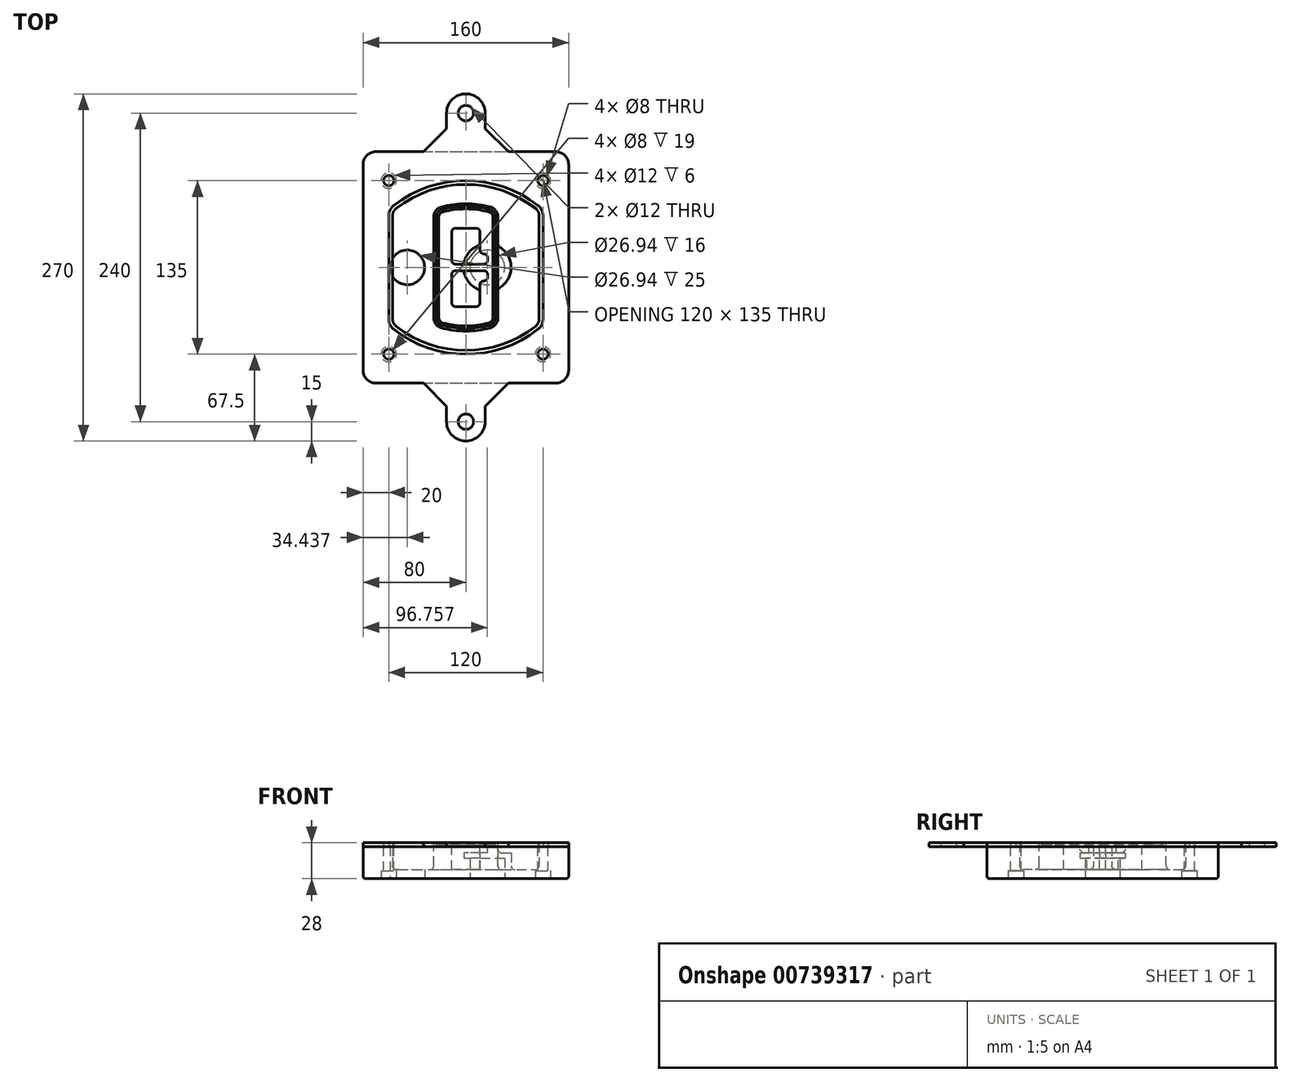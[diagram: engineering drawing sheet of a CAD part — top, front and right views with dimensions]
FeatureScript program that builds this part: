
annotation { "Feature Type Name" : "Feature", "Feature Type Description" : "" }
export const myFeature = defineFeature(function(context is Context, id is Id, definition is map)
    precondition{}
    {
        {
            var Q0;
            Q0=qCreatedBy(makeId("Top.planeOp"),FACE);
            var sketch = newSketch(context, id + "F0", { "sketchPlane" : qUnion([Q0])});
            skPoint(sketch, "E0.rect.middle", {"position": v(0, 0) * mm});
            skLineSegment(sketch, "E1.bottom", {"start": v(-70, -90) * mm, "end": v(70, -90) * mm});
            skLineSegment(sketch, "E1.top", {"start": v(-70, 90) * mm, "end": v(70, 90) * mm});
            skLineSegment(sketch, "E1.left", {"start": v(-80, -80) * mm, "end": v(-80, 80) * mm});
            skLineSegment(sketch, "E1.right", {"start": v(80, -80) * mm, "end": v(80, 80) * mm});
            skLineSegment(sketch, "E2", {"start": v(-80, 90) * mm, "end": v(80, -90) * mm, "construction": true});
            skLineSegment(sketch, "E3", {"start": v(80, 90) * mm, "end": v(-80, -90) * mm, "construction": true});
            skCircle(sketch, "E4", {"center": v(-60, 67.5) * mm, "radius": 4 * mm});
            skCircle(sketch, "E5", {"center": v(60, 67.5) * mm, "radius": 4 * mm});
            skCircle(sketch, "E6", {"center": v(60, -67.5) * mm, "radius": 4 * mm});
            skCircle(sketch, "E7", {"center": v(-60, -67.5) * mm, "radius": 4 * mm});
            skLineSegment(sketch, "E8", {"start": v(-60, 67.5) * mm, "end": v(60, 67.5) * mm, "construction": true});
            skLineSegment(sketch, "E9", {"start": v(60, 67.5) * mm, "end": v(60, -67.5) * mm, "construction": true});
            skLineSegment(sketch, "E10", {"start": v(60, -67.5) * mm, "end": v(-60, -67.5) * mm, "construction": true});
            skLineSegment(sketch, "E11", {"start": v(-60, -67.5) * mm, "end": v(-60, 67.5) * mm, "construction": true});
            skLineSegment(sketch, "E12", {"start": v(-60, 40.3) * mm, "end": v(-60, -40.3) * mm});
            skLineSegment(sketch, "E13", {"start": v(60, 40.3) * mm, "end": v(60, -40.3) * mm});
            skArc(sketch, "E14", {"start": v(56.15, 48.18) * mm, "mid": v(0, 67.5) * mm, "end": v(-56.15, 48.18) * mm});
            skArc(sketch, "E15", {"start": v(-56.15, -48.18) * mm, "mid": v(0, -67.5) * mm, "end": v(56.15, -48.18) * mm});
            skLineSegment(sketch, "E16", {"start": v(-60, 0) * mm, "end": v(60, 0) * mm, "construction": true});
            skPoint(sketch, "E17.visualSharp", {"position": v(-60, -45) * mm});
            skArc(sketch, "E17.filletArc", {"start": v(-60, -40.3) * mm, "mid": v(-58.99, -44.68) * mm, "end": v(-56.15, -48.18) * mm});
            skPoint(sketch, "E18.visualSharp", {"position": v(-60, 45) * mm});
            skArc(sketch, "E18.filletArc", {"start": v(-56.15, 48.18) * mm, "mid": v(-58.99, 44.68) * mm, "end": v(-60, 40.3) * mm});
            skPoint(sketch, "E19.visualSharp", {"position": v(60, 45) * mm});
            skArc(sketch, "E19.filletArc", {"start": v(60, 40.3) * mm, "mid": v(58.99, 44.68) * mm, "end": v(56.15, 48.18) * mm});
            skPoint(sketch, "E20.visualSharp", {"position": v(60, -45) * mm});
            skArc(sketch, "E20.filletArc", {"start": v(56.15, -48.18) * mm, "mid": v(58.99, -44.68) * mm, "end": v(60, -40.3) * mm});
            skPoint(sketch, "E21.visualSharp", {"position": v(-80, 90) * mm});
            skArc(sketch, "E21.filletArc", {"start": v(-70, 90) * mm, "mid": v(-77.07, 87.07) * mm, "end": v(-80, 80) * mm});
            skPoint(sketch, "E22.visualSharp", {"position": v(80, 90) * mm});
            skArc(sketch, "E22.filletArc", {"start": v(80, 80) * mm, "mid": v(77.07, 87.07) * mm, "end": v(70, 90) * mm});
            skPoint(sketch, "E23.visualSharp", {"position": v(80, -90) * mm});
            skArc(sketch, "E23.filletArc", {"start": v(70, -90) * mm, "mid": v(77.07, -87.07) * mm, "end": v(80, -80) * mm});
            skPoint(sketch, "E24.visualSharp", {"position": v(-80, -90) * mm});
            skArc(sketch, "E24.filletArc", {"start": v(-80, -80) * mm, "mid": v(-77.07, -87.07) * mm, "end": v(-70, -90) * mm});
            skArc(sketch, "E25.0", {"start": v(57, 40.3) * mm, "mid": v(56.3, 43.36) * mm, "end": v(54.3, 45.81) * mm});
            skLineSegment(sketch, "E25.1", {"start": v(57, 40.3) * mm, "end": v(57, -40.3) * mm});
            skArc(sketch, "E25.2", {"start": v(54.3, -45.81) * mm, "mid": v(56.3, -43.36) * mm, "end": v(57, -40.3) * mm});
            skArc(sketch, "E25.3", {"start": v(-54.3, -45.81) * mm, "mid": v(0, -64.5) * mm, "end": v(54.3, -45.81) * mm});
            skArc(sketch, "E25.4", {"start": v(-57, -40.3) * mm, "mid": v(-56.3, -43.36) * mm, "end": v(-54.3, -45.81) * mm});
            skArc(sketch, "E25.5", {"start": v(54.3, 45.81) * mm, "mid": v(0, 64.5) * mm, "end": v(-54.3, 45.81) * mm});
            skLineSegment(sketch, "E25.6", {"start": v(-57, 40.3) * mm, "end": v(-57, -40.3) * mm});
            skArc(sketch, "E25.7", {"start": v(-54.3, 45.81) * mm, "mid": v(-56.3, 43.36) * mm, "end": v(-57, 40.3) * mm});
            skArc(sketch, "E26.0", {"start": v(-58.62, 51.33) * mm, "mid": v(-62.58, 46.43) * mm, "end": v(-64, 40.3) * mm});
            skArc(sketch, "E26.1", {"start": v(58.62, 51.33) * mm, "mid": v(0, 71.5) * mm, "end": v(-58.62, 51.33) * mm});
            skArc(sketch, "E26.2", {"start": v(64, 40.3) * mm, "mid": v(62.58, 46.43) * mm, "end": v(58.62, 51.33) * mm});
            skLineSegment(sketch, "E26.3", {"start": v(64, 40.3) * mm, "end": v(64, -40.3) * mm});
            skArc(sketch, "E26.4", {"start": v(58.62, -51.33) * mm, "mid": v(62.58, -46.43) * mm, "end": v(64, -40.3) * mm});
            skLineSegment(sketch, "E26.5", {"start": v(-64, 40.3) * mm, "end": v(-64, -40.3) * mm});
            skArc(sketch, "E26.6", {"start": v(-58.62, -51.33) * mm, "mid": v(0, -71.5) * mm, "end": v(58.62, -51.33) * mm});
            skArc(sketch, "E26.7", {"start": v(-64, -40.3) * mm, "mid": v(-62.58, -46.43) * mm, "end": v(-58.62, -51.33) * mm});
            skSolve(sketch);
        }
        {
            var Q0;
            Q0=makeQuery(id+"F0.imprint","IMPRINT",FACE,{"disambiguationData":[TD([[makeQuery(id+"F0.imprint","IMPRINT",EDGE,{"derivedFrom":sQuery(id+"F0.wireOp",EDGE,"E1.bottom")}),1.0]])]});
            var Q1;
            Q1=makeQuery(id+"F0.imprint","IMPRINT",FACE,{"disambiguationData":[TD([[makeQuery(id+"F0.imprint","IMPRINT",EDGE,{"derivedFrom":sQuery(id+"F0.wireOp",EDGE,"E12")}),1.0]])]});
            var Q2;
            Q2=makeQuery(id+"F0.imprint","IMPRINT",FACE,{"disambiguationData":[TD([[makeQuery(id+"F0.imprint","IMPRINT",EDGE,{"derivedFrom":sQuery(id+"F0.wireOp",EDGE,"E25.0")}),1.0]])]});
            var Q3;
            Q3=makeQuery(id+"F0.imprint","IMPRINT",FACE,{"disambiguationData":[TD([[makeQuery(id+"F0.imprint","IMPRINT",EDGE,{"derivedFrom":sQuery(id+"F0.wireOp",EDGE,"E12")}),-1.0]])]});
            extrude(context, id + "F1", {"entities" : qUnion([Q0, Q1, Q2, Q3]), "oppositeDirection" : true, "depth" : 25 * mm});
        }
        {
            var Q0;
            Q0=makeQuery(id+"F0.imprint","IMPRINT",FACE,{"disambiguationData":[TD([[makeQuery(id+"F0.imprint","IMPRINT",EDGE,{"derivedFrom":sQuery(id+"F0.wireOp",EDGE,"E12")}),1.0]])]});
            extrude(context, id + "F2", {"entities" : qUnion([Q0]), "operationType" : NewBodyOperationType.ADD, "depth" : 3 * mm});
        }
        {
            var Q0;
            Q0=makeQuery(id+"F0.imprint","IMPRINT",FACE,{"disambiguationData":[TD([[makeQuery(id+"F0.imprint","IMPRINT",EDGE,{"derivedFrom":sQuery(id+"F0.wireOp",EDGE,"E25.0")}),1.0]])]});
            extrude(context, id + "F3", {"entities" : qUnion([Q0]), "operationType" : NewBodyOperationType.REMOVE, "oppositeDirection" : true, "depth" : 18 * mm});
        }
        {
            var Q0;
            Q0=makeQuery(id+"F2.opExtrude","CAP_FACE",FACE,{"disambiguationData":[OSD([sQuery(id+"F0.wireOp",EDGE,"E12"),sQuery(id+"F0.wireOp",EDGE,"E13"),sQuery(id+"F0.wireOp",EDGE,"E14"),sQuery(id+"F0.wireOp",EDGE,"E15"),sQuery(id+"F0.wireOp",EDGE,"E17.filletArc"),sQuery(id+"F0.wireOp",EDGE,"E18.filletArc"),sQuery(id+"F0.wireOp",EDGE,"E19.filletArc"),sQuery(id+"F0.wireOp",EDGE,"E20.filletArc"),sQuery(id+"F0.wireOp",EDGE,"E25.0"),sQuery(id+"F0.wireOp",EDGE,"E25.1"),sQuery(id+"F0.wireOp",EDGE,"E25.2"),sQuery(id+"F0.wireOp",EDGE,"E25.3"),sQuery(id+"F0.wireOp",EDGE,"E25.4"),sQuery(id+"F0.wireOp",EDGE,"E25.5"),sQuery(id+"F0.wireOp",EDGE,"E25.6"),sQuery(id+"F0.wireOp",EDGE,"E25.7")])],"isStart":false});
            var sketch = newSketch(context, id + "F4", { "sketchPlane" : qUnion([Q0])});
            skArc(sketch, "E27.0", {"start": v(-19.08, -46.97) * mm, "mid": v(0, -49.5) * mm, "end": v(19.08, -46.97) * mm});
            skArc(sketch, "E28.0", {"start": v(19.08, 46.97) * mm, "mid": v(0, 49.5) * mm, "end": v(-19.08, 46.97) * mm});
            skLineSegment(sketch, "E29", {"start": v(-25, 39.25) * mm, "end": v(-25, -39.25) * mm});
            skLineSegment(sketch, "E30", {"start": v(25, 39.25) * mm, "end": v(25, -39.25) * mm});
            skLineSegment(sketch, "E31", {"start": v(-25, 45.1) * mm, "end": v(25, 45.1) * mm, "construction": true});
            skLineSegment(sketch, "E32", {"start": v(-25, -45.1) * mm, "end": v(25, -45.1) * mm, "construction": true});
            skPoint(sketch, "E33.visualSharp", {"position": v(-25, 45.1) * mm});
            skArc(sketch, "E33.filletArc", {"start": v(-19.08, 46.97) * mm, "mid": v(-23.35, 44.11) * mm, "end": v(-25, 39.25) * mm});
            skPoint(sketch, "E34.visualSharp", {"position": v(25, 45.1) * mm});
            skArc(sketch, "E34.filletArc", {"start": v(25, 39.25) * mm, "mid": v(23.35, 44.11) * mm, "end": v(19.08, 46.97) * mm});
            skPoint(sketch, "E35.visualSharp", {"position": v(25, -45.1) * mm});
            skArc(sketch, "E35.filletArc", {"start": v(19.08, -46.97) * mm, "mid": v(23.35, -44.11) * mm, "end": v(25, -39.25) * mm});
            skPoint(sketch, "E36.visualSharp", {"position": v(-25, -45.1) * mm});
            skArc(sketch, "E36.filletArc", {"start": v(-25, -39.25) * mm, "mid": v(-23.35, -44.11) * mm, "end": v(-19.08, -46.97) * mm});
            skArc(sketch, "E37.0", {"start": v(54.3, 45.81) * mm, "mid": v(0, 64.5) * mm, "end": v(-54.3, 45.81) * mm});
            skArc(sketch, "E37.1", {"start": v(-54.3, 45.81) * mm, "mid": v(-56.3, 43.36) * mm, "end": v(-57, 40.3) * mm});
            skLineSegment(sketch, "E37.2", {"start": v(-57, 40.3) * mm, "end": v(-57, -40.3) * mm});
            skArc(sketch, "E37.3", {"start": v(-57, -40.3) * mm, "mid": v(-56.3, -43.36) * mm, "end": v(-54.3, -45.81) * mm});
            skArc(sketch, "E37.4", {"start": v(-54.3, -45.81) * mm, "mid": v(0, -64.5) * mm, "end": v(54.3, -45.81) * mm});
            skArc(sketch, "E37.5", {"start": v(54.3, -45.81) * mm, "mid": v(56.3, -43.36) * mm, "end": v(57, -40.3) * mm});
            skLineSegment(sketch, "E37.6", {"start": v(57, 40.3) * mm, "end": v(57, -40.3) * mm});
            skArc(sketch, "E37.7", {"start": v(57, 40.3) * mm, "mid": v(56.3, 43.36) * mm, "end": v(54.3, 45.81) * mm});
            skLineSegment(sketch, "E38.0", {"start": v(23, 39.25) * mm, "end": v(23, -39.25) * mm});
            skArc(sketch, "E38.1", {"start": v(18.56, -45.04) * mm, "mid": v(21.76, -42.9) * mm, "end": v(23, -39.25) * mm});
            skArc(sketch, "E38.2", {"start": v(-18.56, -45.04) * mm, "mid": v(0, -47.5) * mm, "end": v(18.56, -45.04) * mm});
            skArc(sketch, "E38.3", {"start": v(-23, -39.25) * mm, "mid": v(-21.76, -42.9) * mm, "end": v(-18.56, -45.04) * mm});
            skLineSegment(sketch, "E38.4", {"start": v(-23, 39.25) * mm, "end": v(-23, -39.25) * mm});
            skArc(sketch, "E38.5", {"start": v(23, 39.25) * mm, "mid": v(21.76, 42.9) * mm, "end": v(18.56, 45.04) * mm});
            skArc(sketch, "E38.6", {"start": v(-18.56, 45.04) * mm, "mid": v(-21.76, 42.9) * mm, "end": v(-23, 39.25) * mm});
            skArc(sketch, "E38.7", {"start": v(18.56, 45.04) * mm, "mid": v(0, 47.5) * mm, "end": v(-18.56, 45.04) * mm});
            skArc(sketch, "E39.0", {"start": v(21, 39.25) * mm, "mid": v(20.18, 41.68) * mm, "end": v(18.04, 43.1) * mm});
            skLineSegment(sketch, "E39.1", {"start": v(21, 39.25) * mm, "end": v(21, -39.25) * mm});
            skArc(sketch, "E39.2", {"start": v(18.04, -43.1) * mm, "mid": v(20.18, -41.68) * mm, "end": v(21, -39.25) * mm});
            skArc(sketch, "E39.3", {"start": v(-18.04, -43.1) * mm, "mid": v(0, -45.5) * mm, "end": v(18.04, -43.1) * mm});
            skArc(sketch, "E39.4", {"start": v(-21, -39.25) * mm, "mid": v(-20.18, -41.68) * mm, "end": v(-18.04, -43.1) * mm});
            skArc(sketch, "E39.5", {"start": v(18.04, 43.1) * mm, "mid": v(0, 45.5) * mm, "end": v(-18.04, 43.1) * mm});
            skLineSegment(sketch, "E39.6", {"start": v(-21, 39.25) * mm, "end": v(-21, -39.25) * mm});
            skArc(sketch, "E39.7", {"start": v(-18.04, 43.1) * mm, "mid": v(-20.18, 41.68) * mm, "end": v(-21, 39.25) * mm});
            skLineSegment(sketch, "E40", {"start": v(-25, 0) * mm, "end": v(25, 0) * mm, "construction": true});
            skLineSegment(sketch, "E41", {"start": v(-11, 5.5) * mm, "end": v(-11, 27.5) * mm});
            skLineSegment(sketch, "E42", {"start": v(-8, 30.5) * mm, "end": v(8, 30.5) * mm});
            skLineSegment(sketch, "E43", {"start": v(11, 27.5) * mm, "end": v(11, 13.5) * mm});
            skLineSegment(sketch, "E44", {"start": v(14, 10.5) * mm, "end": v(14, 10.5) * mm});
            skLineSegment(sketch, "E45", {"start": v(17, 7.5) * mm, "end": v(17, 5.5) * mm});
            skLineSegment(sketch, "E46", {"start": v(14, 2.5) * mm, "end": v(-8, 2.5) * mm});
            skPoint(sketch, "E47.visualSharp", {"position": v(-11, 30.5) * mm});
            skArc(sketch, "E47.filletArc", {"start": v(-8, 30.5) * mm, "mid": v(-10.12, 29.62) * mm, "end": v(-11, 27.5) * mm});
            skPoint(sketch, "E48.visualSharp", {"position": v(11, 30.5) * mm});
            skArc(sketch, "E48.filletArc", {"start": v(11, 27.5) * mm, "mid": v(10.12, 29.62) * mm, "end": v(8, 30.5) * mm});
            skPoint(sketch, "E49.visualSharp", {"position": v(11, 10.5) * mm});
            skArc(sketch, "E49.filletArc", {"start": v(11, 13.5) * mm, "mid": v(11.88, 11.38) * mm, "end": v(14, 10.5) * mm});
            skPoint(sketch, "E50.visualSharp", {"position": v(17, 10.5) * mm});
            skArc(sketch, "E50.filletArc", {"start": v(17, 7.5) * mm, "mid": v(16.12, 9.62) * mm, "end": v(14, 10.5) * mm});
            skPoint(sketch, "E51.visualSharp", {"position": v(17, 2.5) * mm});
            skArc(sketch, "E51.filletArc", {"start": v(14, 2.5) * mm, "mid": v(16.12, 3.38) * mm, "end": v(17, 5.5) * mm});
            skPoint(sketch, "E52.visualSharp", {"position": v(-11, 2.5) * mm});
            skArc(sketch, "E52.filletArc", {"start": v(-11, 5.5) * mm, "mid": v(-10.12, 3.38) * mm, "end": v(-8, 2.5) * mm});
            skLineSegment(sketch, "E53.0.MirrorCS", {"start": v(14, -2.5) * mm, "end": v(-8, -2.5) * mm});
            skArc(sketch, "E54.0.MirrorCS", {"start": v(-11, -5.5) * mm, "mid": v(-10.12, -3.38) * mm, "end": v(-8, -2.5) * mm});
            skLineSegment(sketch, "E55.0.MirrorCS", {"start": v(-11, -5.5) * mm, "end": v(-11, -27.5) * mm});
            skArc(sketch, "E56.0.MirrorCS", {"start": v(-8, -30.5) * mm, "mid": v(-10.12, -29.62) * mm, "end": v(-11, -27.5) * mm});
            skLineSegment(sketch, "E57.0.MirrorCS", {"start": v(-8, -30.5) * mm, "end": v(8, -30.5) * mm});
            skArc(sketch, "E58.0.MirrorCS", {"start": v(11, -27.5) * mm, "mid": v(10.12, -29.62) * mm, "end": v(8, -30.5) * mm});
            skLineSegment(sketch, "E59.0.MirrorCS", {"start": v(11, -27.5) * mm, "end": v(11, -13.5) * mm});
            skArc(sketch, "E60.0.MirrorCS", {"start": v(11, -13.5) * mm, "mid": v(11.88, -11.38) * mm, "end": v(14, -10.5) * mm});
            skArc(sketch, "E61.0.MirrorCS", {"start": v(17, -7.5) * mm, "mid": v(16.12, -9.62) * mm, "end": v(14, -10.5) * mm});
            skLineSegment(sketch, "E62.0.MirrorCS", {"start": v(17, -7.5) * mm, "end": v(17, -5.5) * mm});
            skArc(sketch, "E63.0.MirrorCS", {"start": v(14, -2.5) * mm, "mid": v(16.12, -3.38) * mm, "end": v(17, -5.5) * mm});
            skSolve(sketch);
        }
        {
            var Q0;
            Q0=makeQuery(id+"F4.imprint","IMPRINT",FACE,{"disambiguationData":[TD([[makeQuery(id+"F4.imprint","IMPRINT",EDGE,{"derivedFrom":sQuery(id+"F4.wireOp",EDGE,"E27.0")}),1.0]])]});
            var Q1;
            Q1=makeQuery(id+"F4.imprint","IMPRINT",FACE,{"disambiguationData":[TD([[makeQuery(id+"F4.imprint","IMPRINT",EDGE,{"derivedFrom":sQuery(id+"F4.wireOp",EDGE,"E38.0")}),-1.0]])]});
            var Q2;
            Q2=makeQuery(id+"F4.imprint","IMPRINT",FACE,{"disambiguationData":[TD([[makeQuery(id+"F4.imprint","IMPRINT",EDGE,{"derivedFrom":sQuery(id+"F4.wireOp",EDGE,"E39.0")}),1.0]])]});
            extrude(context, id + "F5", {"entities" : qUnion([Q0, Q1, Q2]), "operationType" : NewBodyOperationType.ADD, "endBound" : BoundingType.UP_TO_NEXT, "oppositeDirection" : true, "depth" : 25 * mm});
        }
        {
            var Q0;
            Q0=makeQuery(id+"F4.imprint","IMPRINT",FACE,{"disambiguationData":[TD([[makeQuery(id+"F4.imprint","IMPRINT",EDGE,{"derivedFrom":sQuery(id+"F4.wireOp",EDGE,"E38.0")}),-1.0]])]});
            extrude(context, id + "F6", {"entities" : qUnion([Q0]), "operationType" : NewBodyOperationType.REMOVE, "oppositeDirection" : true, "depth" : 2 * mm});
        }
        {
            var Q0;
            Q0=makeQuery(id+"F1.opExtrude","CAP_FACE",FACE,{"disambiguationData":[OSD([sQuery(id+"F0.wireOp",EDGE,"E1.bottom"),sQuery(id+"F0.wireOp",EDGE,"E1.top"),sQuery(id+"F0.wireOp",EDGE,"E1.left"),sQuery(id+"F0.wireOp",EDGE,"E1.right"),sQuery(id+"F0.wireOp",EDGE,"E4"),sQuery(id+"F0.wireOp",EDGE,"E5"),sQuery(id+"F0.wireOp",EDGE,"E6"),sQuery(id+"F0.wireOp",EDGE,"E7"),sQuery(id+"F0.wireOp",EDGE,"E21.filletArc"),sQuery(id+"F0.wireOp",EDGE,"E22.filletArc"),sQuery(id+"F0.wireOp",EDGE,"E23.filletArc"),sQuery(id+"F0.wireOp",EDGE,"E24.filletArc")])],"isStart":false});
            var sketch = newSketch(context, id + "F7", { "sketchPlane" : qUnion([Q0])});
            skCircle(sketch, "E64", {"center": v(16.76, 0) * mm, "radius": 13.47 * mm});
            skCircle(sketch, "E65", {"center": v(-45.56, 0) * mm, "radius": 13.47 * mm});
            skLineSegment(sketch, "E66", {"start": v(80, 0) * mm, "end": v(-80, 0) * mm});
            skCircle(sketch, "E67", {"center": v(16.76, 0) * mm, "radius": 18.47 * mm});
            skCircle(sketch, "E68", {"center": v(60, -67.5) * mm, "radius": 6 * mm});
            skCircle(sketch, "E69", {"center": v(-60, -67.5) * mm, "radius": 6 * mm});
            skCircle(sketch, "E70", {"center": v(-60, 67.5) * mm, "radius": 6 * mm});
            skCircle(sketch, "E71", {"center": v(60, 67.5) * mm, "radius": 6 * mm});
            skSolve(sketch);
        }
        {
            var Q0;
            {var subQ1=sQuery(id+"F7.wireOp",EDGE,"E66");var subQ4=sQuery(id+"F7.wireOp",EDGE,"E64");var subQ6=makeQuery(id+"F7.imprint","INTERSECT",VERTEX,{"disambiguationData":[OD(0.0)],"derivedFrom":[subQ4,subQ1]});Q0=makeQuery(id+"F7.imprint","IMPRINT",FACE,{"disambiguationData":[TD([[makeQuery(id+"F7.imprint","IMPRINT",EDGE,{"disambiguationData":[TD([[subQ6,-1.0]])],"derivedFrom":subQ4}),-1.0]])]});}
            var Q1;
            {var subQ0=sQuery(id+"F7.wireOp",EDGE,"E66");var subQ1=sQuery(id+"F7.wireOp",EDGE,"E64");var subQ3=makeQuery(id+"F7.imprint","INTERSECT",VERTEX,{"disambiguationData":[OD(0.0)],"derivedFrom":[subQ1,subQ0]});Q1=makeQuery(id+"F7.imprint","IMPRINT",FACE,{"disambiguationData":[TD([[makeQuery(id+"F7.imprint","IMPRINT",EDGE,{"disambiguationData":[TD([[subQ3,-1.0]])],"derivedFrom":subQ1}),1.0]])]});}
            var Q2;
            {var subQ0=sQuery(id+"F7.wireOp",EDGE,"E66");var subQ1=sQuery(id+"F7.wireOp",EDGE,"E64");var subQ3=makeQuery(id+"F7.imprint","INTERSECT",VERTEX,{"disambiguationData":[OD(0.0)],"derivedFrom":[subQ1,subQ0]});Q2=makeQuery(id+"F7.imprint","IMPRINT",FACE,{"disambiguationData":[TD([[makeQuery(id+"F7.imprint","IMPRINT",EDGE,{"disambiguationData":[TD([[subQ3,1.0]])],"derivedFrom":subQ1}),1.0]])]});}
            var Q3;
            {var subQ1=sQuery(id+"F7.wireOp",EDGE,"E66");var subQ4=sQuery(id+"F7.wireOp",EDGE,"E64");var subQ6=makeQuery(id+"F7.imprint","INTERSECT",VERTEX,{"disambiguationData":[OD(0.0)],"derivedFrom":[subQ4,subQ1]});Q3=makeQuery(id+"F7.imprint","IMPRINT",FACE,{"disambiguationData":[TD([[makeQuery(id+"F7.imprint","IMPRINT",EDGE,{"disambiguationData":[TD([[subQ6,1.0]])],"derivedFrom":subQ4}),-1.0]])]});}
            extrude(context, id + "F8", {"entities" : qUnion([Q0, Q1, Q2, Q3]), "operationType" : NewBodyOperationType.ADD, "oppositeDirection" : true, "depth" : 20 * mm});
        }
        {
            var Q0;
            {var subQ0=sQuery(id+"F7.wireOp",EDGE,"E66");var subQ1=sQuery(id+"F7.wireOp",EDGE,"E64");var subQ3=makeQuery(id+"F7.imprint","INTERSECT",VERTEX,{"disambiguationData":[OD(0.0)],"derivedFrom":[subQ1,subQ0]});Q0=makeQuery(id+"F7.imprint","IMPRINT",FACE,{"disambiguationData":[TD([[makeQuery(id+"F7.imprint","IMPRINT",EDGE,{"disambiguationData":[TD([[subQ3,-1.0]])],"derivedFrom":subQ1}),1.0]])]});}
            var Q1;
            {var subQ0=sQuery(id+"F7.wireOp",EDGE,"E66");var subQ1=sQuery(id+"F7.wireOp",EDGE,"E64");var subQ3=makeQuery(id+"F7.imprint","INTERSECT",VERTEX,{"disambiguationData":[OD(0.0)],"derivedFrom":[subQ1,subQ0]});Q1=makeQuery(id+"F7.imprint","IMPRINT",FACE,{"disambiguationData":[TD([[makeQuery(id+"F7.imprint","IMPRINT",EDGE,{"disambiguationData":[TD([[subQ3,1.0]])],"derivedFrom":subQ1}),1.0]])]});}
            extrude(context, id + "F9", {"entities" : qUnion([Q0, Q1]), "operationType" : NewBodyOperationType.REMOVE, "oppositeDirection" : true, "depth" : 16 * mm});
        }
        {
            var Q0;
            {var subQ0=sQuery(id+"F7.wireOp",EDGE,"E66");var subQ1=sQuery(id+"F7.wireOp",EDGE,"E65");var subQ3=makeQuery(id+"F7.imprint","INTERSECT",VERTEX,{"disambiguationData":[OD(0.0)],"derivedFrom":[subQ1,subQ0]});Q0=makeQuery(id+"F7.imprint","IMPRINT",FACE,{"disambiguationData":[TD([[makeQuery(id+"F7.imprint","IMPRINT",EDGE,{"disambiguationData":[TD([[subQ3,-1.0]])],"derivedFrom":subQ1}),1.0]])]});}
            var Q1;
            {var subQ0=sQuery(id+"F7.wireOp",EDGE,"E66");var subQ1=sQuery(id+"F7.wireOp",EDGE,"E65");var subQ3=makeQuery(id+"F7.imprint","INTERSECT",VERTEX,{"disambiguationData":[OD(0.0)],"derivedFrom":[subQ1,subQ0]});Q1=makeQuery(id+"F7.imprint","IMPRINT",FACE,{"disambiguationData":[TD([[makeQuery(id+"F7.imprint","IMPRINT",EDGE,{"disambiguationData":[TD([[subQ3,1.0]])],"derivedFrom":subQ1}),1.0]])]});}
            extrude(context, id + "F10", {"entities" : qUnion([Q0, Q1]), "operationType" : NewBodyOperationType.REMOVE, "oppositeDirection" : true, "depth" : 25 * mm});
        }
        {
            var Q0;
            Q0=makeQuery(id+"F7.imprint","IMPRINT",FACE,{"disambiguationData":[TD([[makeQuery(id+"F7.imprint","IMPRINT",EDGE,{"derivedFrom":sQuery(id+"F7.wireOp",EDGE,"E68")}),1.0]])]});
            var Q1;
            Q1=makeQuery(id+"F7.imprint","IMPRINT",FACE,{"disambiguationData":[TD([[makeQuery(id+"F7.imprint","IMPRINT",EDGE,{"derivedFrom":makeQuery(id+"F1.opExtrude","CAP_EDGE",EDGE,{"disambiguationData":[OSD([sQuery(id+"F0.wireOp",EDGE,"E5")])],"isStart":false})}),-1.0]])]});
            var Q2;
            Q2=makeQuery(id+"F7.imprint","IMPRINT",FACE,{"disambiguationData":[TD([[makeQuery(id+"F7.imprint","IMPRINT",EDGE,{"derivedFrom":sQuery(id+"F7.wireOp",EDGE,"E69")}),1.0]])]});
            var Q3;
            Q3=makeQuery(id+"F7.imprint","IMPRINT",FACE,{"disambiguationData":[TD([[makeQuery(id+"F7.imprint","IMPRINT",EDGE,{"derivedFrom":makeQuery(id+"F1.opExtrude","CAP_EDGE",EDGE,{"disambiguationData":[OSD([sQuery(id+"F0.wireOp",EDGE,"E4")])],"isStart":false})}),-1.0]])]});
            var Q4;
            Q4=makeQuery(id+"F7.imprint","IMPRINT",FACE,{"disambiguationData":[TD([[makeQuery(id+"F7.imprint","IMPRINT",EDGE,{"derivedFrom":sQuery(id+"F7.wireOp",EDGE,"E70")}),1.0]])]});
            var Q5;
            Q5=makeQuery(id+"F7.imprint","IMPRINT",FACE,{"disambiguationData":[TD([[makeQuery(id+"F7.imprint","IMPRINT",EDGE,{"derivedFrom":makeQuery(id+"F1.opExtrude","CAP_EDGE",EDGE,{"disambiguationData":[OSD([sQuery(id+"F0.wireOp",EDGE,"E7")])],"isStart":false})}),-1.0]])]});
            var Q6;
            Q6=makeQuery(id+"F7.imprint","IMPRINT",FACE,{"disambiguationData":[TD([[makeQuery(id+"F7.imprint","IMPRINT",EDGE,{"derivedFrom":sQuery(id+"F7.wireOp",EDGE,"E71")}),1.0]])]});
            var Q7;
            Q7=makeQuery(id+"F7.imprint","IMPRINT",FACE,{"disambiguationData":[TD([[makeQuery(id+"F7.imprint","IMPRINT",EDGE,{"derivedFrom":makeQuery(id+"F1.opExtrude","CAP_EDGE",EDGE,{"disambiguationData":[OSD([sQuery(id+"F0.wireOp",EDGE,"E6")])],"isStart":false})}),-1.0]])]});
            var Q8;
            Q8 = qSketchRegion(id + "F16", true);
            extrude(context, id + "F11", {"entities" : qUnion([Q0, Q1, Q2, Q3, Q4, Q5, Q6, Q7, Q8]), "operationType" : NewBodyOperationType.REMOVE, "oppositeDirection" : true, "depth" : 6 * mm, "offsetDistance" : 25 * mm});
        }
        {
            var Q0;
            Q0=makeQuery(id+"F9.boolean.opBoolean","COPY",FACE,{"derivedFrom":makeQuery(id+"F9.opExtrude","CAP_FACE",FACE,{"disambiguationData":[OSD([sQuery(id+"F7.wireOp",EDGE,"E64")])],"isStart":false})});
            var sketch = newSketch(context, id + "F12", { "sketchPlane" : qUnion([Q0])});
            skArc(sketch, "E72.0", {"start": v(11, 17.55) * mm, "mid": v(2.57, 11.82) * mm, "end": v(-1.54, 2.5) * mm});
            skArc(sketch, "E72.1", {"start": v(-1.54, -2.5) * mm, "mid": v(2.57, -11.82) * mm, "end": v(11, -17.55) * mm});
            skLineSegment(sketch, "E73", {"start": v(-1.54, -2.5) * mm, "end": v(14, -2.5) * mm});
            skLineSegment(sketch, "E74.0", {"start": v(14, 2.5) * mm, "end": v(-1.54, 2.5) * mm});
            skArc(sketch, "E74.1", {"start": v(14, 2.5) * mm, "mid": v(16.12, 3.38) * mm, "end": v(17, 5.5) * mm});
            skLineSegment(sketch, "E74.2", {"start": v(17, 7.5) * mm, "end": v(17, 5.5) * mm});
            skArc(sketch, "E74.3", {"start": v(17, 7.5) * mm, "mid": v(16.12, 9.62) * mm, "end": v(14, 10.5) * mm});
            skArc(sketch, "E74.4", {"start": v(11, 13.5) * mm, "mid": v(11.88, 11.38) * mm, "end": v(14, 10.5) * mm});
            skLineSegment(sketch, "E74.5", {"start": v(11, 17.55) * mm, "end": v(11, 13.5) * mm});
            skLineSegment(sketch, "E74.7", {"start": v(14, -2.5) * mm, "end": v(-1.54, -2.5) * mm});
            skArc(sketch, "E74.8", {"start": v(14, -2.5) * mm, "mid": v(16.12, -3.38) * mm, "end": v(17, -5.5) * mm});
            skLineSegment(sketch, "E74.9", {"start": v(17, -7.5) * mm, "end": v(17, -5.5) * mm});
            skArc(sketch, "E74.10", {"start": v(17, -7.5) * mm, "mid": v(16.12, -9.62) * mm, "end": v(14, -10.5) * mm});
            skArc(sketch, "E74.11", {"start": v(11, -13.5) * mm, "mid": v(11.88, -11.38) * mm, "end": v(14, -10.5) * mm});
            skLineSegment(sketch, "E74.12", {"start": v(11, -17.55) * mm, "end": v(11, -13.5) * mm});
            skPoint(sketch, "E75.orphan", {"position": v(11, -27.5) * mm});
            skPoint(sketch, "E76.orphan", {"position": v(-8, -2.5) * mm});
            skPoint(sketch, "E77.orphan", {"position": v(-8, 2.5) * mm});
            skPoint(sketch, "E78.orphan", {"position": v(11, 27.5) * mm});
            skSolve(sketch);
        }
        {
            var Q0;
            {var subQ7=sQuery(id+"F12.wireOp",EDGE,"E72.0");var subQ14=sQuery(id+"F12.wireOp",EDGE,"E72.1");var subQ16=sQuery(id+"F12.wireOp",EDGE,"E74.1");var subQ18=sQuery(id+"F12.wireOp",EDGE,"E74.8");Q0=qUnion([makeQuery(id+"F12.imprint","IMPRINT",FACE,{"disambiguationData":[TD([[makeQuery(id+"F12.imprint","IMPRINT",EDGE,{"derivedFrom":subQ7}),1.0]])]}),makeQuery(id+"F12.imprint","IMPRINT",FACE,{"disambiguationData":[TD([[makeQuery(id+"F12.imprint","IMPRINT",EDGE,{"derivedFrom":subQ14}),1.0]])]}),makeQuery(id+"F12.imprint","IMPRINT",FACE,{"disambiguationData":[TD([[makeQuery(id+"F12.imprint","IMPRINT",EDGE,{"derivedFrom":subQ16}),1.0]])]}),makeQuery(id+"F12.imprint","IMPRINT",FACE,{"disambiguationData":[TD([[makeQuery(id+"F12.imprint","IMPRINT",EDGE,{"derivedFrom":subQ18}),-1.0]])]})]);}
            var Q1;
            Q1=makeQuery(id+"F5.boolean.opBoolean","SPLIT",FACE,{"disambiguationData":[TD([makeQuery(id+"F5.opExtrude","SWEPT_FACE",FACE,{"disambiguationData":[OSD([sQuery(id+"F4.wireOp",EDGE,"E41")])]})])],"derivedFrom":makeQuery(id+"F3.boolean.opBoolean","COPY",FACE,{"derivedFrom":makeQuery(id+"F3.opExtrude","CAP_FACE",FACE,{"disambiguationData":[OSD([sQuery(id+"F0.wireOp",EDGE,"E25.0"),sQuery(id+"F0.wireOp",EDGE,"E25.1"),sQuery(id+"F0.wireOp",EDGE,"E25.2"),sQuery(id+"F0.wireOp",EDGE,"E25.3"),sQuery(id+"F0.wireOp",EDGE,"E25.4"),sQuery(id+"F0.wireOp",EDGE,"E25.5"),sQuery(id+"F0.wireOp",EDGE,"E25.6"),sQuery(id+"F0.wireOp",EDGE,"E25.7")])],"isStart":false})})});
            extrude(context, id + "F13", {"entities" : qUnion([Q0]), "operationType" : NewBodyOperationType.REMOVE, "endBound" : BoundingType.UP_TO_SURFACE, "endBoundEntityFace" : qUnion([Q1]), "depth" : 25 * mm});
        }
        {
            var Q0;
            Q0=makeQuery(id+"F3.boolean.opBoolean","COPY",EDGE,{"derivedFrom":makeQuery(id+"F3.opExtrude","CAP_EDGE",EDGE,{"disambiguationData":[OSD([sQuery(id+"F0.wireOp",EDGE,"E25.6")])],"isStart":false})});
            var Q1;
            Q1=makeQuery(id+"F8.boolean.opBoolean","INTERSECT",EDGE,{"derivedFrom":[makeQuery(id+"F5.opExtrude","SWEPT_FACE",FACE,{"disambiguationData":[OSD([sQuery(id+"F4.wireOp",EDGE,"E30")])]}),makeQuery(id+"F8.opExtrude","CAP_FACE",FACE,{"disambiguationData":[OSD([sQuery(id+"F7.wireOp",EDGE,"E67")])],"isStart":false})]});
            var Q2;
            Q2=makeQuery(id+"F8.boolean.opBoolean","INTERSECT",EDGE,{"disambiguationData":[OD(1.0)],"derivedFrom":[makeQuery(id+"F5.opExtrude","SWEPT_FACE",FACE,{"disambiguationData":[OSD([sQuery(id+"F4.wireOp",EDGE,"E30")])]}),makeQuery(id+"F8.opExtrude","SWEPT_FACE",FACE,{"disambiguationData":[OSD([sQuery(id+"F7.wireOp",EDGE,"E67")])]})]});
            var Q3;
            {var subQ0=sQuery(id+"F4.wireOp",EDGE,"E30");Q3=makeQuery(id+"F8.boolean.opBoolean","SPLIT",EDGE,{"disambiguationData":[TD([makeQuery(id+"F5.opExtrude","SWEPT_FACE",FACE,{"disambiguationData":[OSD([sQuery(id+"F4.wireOp",EDGE,"E35.filletArc")])]})])],"derivedFrom":makeQuery(id+"F5.opExtrude","CAP_EDGE",EDGE,{"disambiguationData":[OSD([subQ0])],"isStart":false})});}
            var Q4;
            {var subQ0=sQuery(id+"F0.wireOp",EDGE,"E25.7");var subQ1=sQuery(id+"F0.wireOp",EDGE,"E25.1");var subQ2=sQuery(id+"F0.wireOp",EDGE,"E25.6");var subQ3=sQuery(id+"F0.wireOp",EDGE,"E25.5");var subQ4=sQuery(id+"F0.wireOp",EDGE,"E25.4");var subQ5=sQuery(id+"F0.wireOp",EDGE,"E25.0");var subQ6=sQuery(id+"F0.wireOp",EDGE,"E25.2");var subQ7=sQuery(id+"F0.wireOp",EDGE,"E25.3");Q4=makeQuery(id+"F8.boolean.opBoolean","INTERSECT",EDGE,{"derivedFrom":[makeQuery(id+"F5.boolean.opBoolean","SPLIT",FACE,{"disambiguationData":[TD([makeQuery(id+"F2.opExtrude","SWEPT_FACE",FACE,{"disambiguationData":[OSD([subQ5])]})])],"derivedFrom":makeQuery(id+"F3.boolean.opBoolean","COPY",FACE,{"derivedFrom":makeQuery(id+"F3.opExtrude","CAP_FACE",FACE,{"disambiguationData":[OSD([subQ5,subQ1,subQ6,subQ7,subQ4,subQ3,subQ2,subQ0])],"isStart":false})})}),makeQuery(id+"F8.opExtrude","SWEPT_FACE",FACE,{"disambiguationData":[OSD([sQuery(id+"F7.wireOp",EDGE,"E67")])]})]});}
            var Q5;
            Q5=makeQuery(id+"F8.boolean.opBoolean","INTERSECT",EDGE,{"disambiguationData":[OD(0.0)],"derivedFrom":[makeQuery(id+"F5.opExtrude","SWEPT_FACE",FACE,{"disambiguationData":[OSD([sQuery(id+"F4.wireOp",EDGE,"E30")])]}),makeQuery(id+"F8.opExtrude","SWEPT_FACE",FACE,{"disambiguationData":[OSD([sQuery(id+"F7.wireOp",EDGE,"E67")])]})]});
            fillet(context, id + "F14", {"entities" : qUnion([Q0, Q1, Q2, Q3, Q4, Q5]), "radius" : 3 * mm, "tangentPropagation" : true, "allowEdgeOverflow" : false});
        }
        {
            var Q0;
            Q0=makeQuery(id+"F1.opExtrude","CAP_EDGE",EDGE,{"disambiguationData":[OSD([sQuery(id+"F0.wireOp",EDGE,"E1.bottom")])],"isStart":false});
            fillet(context, id + "F15", {"entities" : qUnion([Q0]), "radius" : 2 * mm, "tangentPropagation" : true, "allowEdgeOverflow" : false});
        }
        {
            var Q0;
            {var subQ0=sQuery(id+"F0.wireOp",EDGE,"E21.filletArc");var subQ1=sQuery(id+"F0.wireOp",EDGE,"E7");var subQ2=sQuery(id+"F0.wireOp",EDGE,"E6");var subQ3=sQuery(id+"F0.wireOp",EDGE,"E5");var subQ4=sQuery(id+"F0.wireOp",EDGE,"E4");var subQ5=sQuery(id+"F0.wireOp",EDGE,"E22.filletArc");var subQ6=sQuery(id+"F0.wireOp",EDGE,"E1.bottom");var subQ7=sQuery(id+"F0.wireOp",EDGE,"E1.right");var subQ8=sQuery(id+"F0.wireOp",EDGE,"E1.top");var subQ9=sQuery(id+"F0.wireOp",EDGE,"E1.left");var subQ10=sQuery(id+"F0.wireOp",EDGE,"E23.filletArc");var subQ11=sQuery(id+"F0.wireOp",EDGE,"E24.filletArc");Q0=makeQuery(id+"F2.boolean.opBoolean","SPLIT",FACE,{"disambiguationData":[TD([makeQuery(id+"F1.opExtrude","SWEPT_FACE",FACE,{"disambiguationData":[OSD([subQ6])]})])],"derivedFrom":makeQuery(id+"F1.opExtrude","CAP_FACE",FACE,{"disambiguationData":[OSD([subQ6,subQ8,subQ9,subQ7,subQ4,subQ3,subQ2,subQ1,subQ0,subQ5,subQ10,subQ11])],"isStart":true})});}
            var sketch = newSketch(context, id + "F16", { "sketchPlane" : qUnion([Q0])});
            skLineSegment(sketch, "E79", {"start": v(-15, 108) * mm, "end": v(-15, 120) * mm});
            skArc(sketch, "E80", {"start": v(15, 120) * mm, "mid": v(0, 135) * mm, "end": v(-15, 120) * mm});
            skLineSegment(sketch, "E81", {"start": v(15, 120) * mm, "end": v(15, 108) * mm});
            skLineSegment(sketch, "E82", {"start": v(15, 108) * mm, "end": v(33, 90) * mm});
            skCircle(sketch, "E83", {"center": v(0, 120) * mm, "radius": 6 * mm});
            skLineSegment(sketch, "E84", {"start": v(-15, 108) * mm, "end": v(-33, 90) * mm});
            skLineSegment(sketch, "E85", {"start": v(0, 90) * mm, "end": v(0, 120) * mm, "construction": true});
            skLineSegment(sketch, "E86.MirrorCS", {"start": v(15, 108) * mm, "end": v(15, 120) * mm});
            skArc(sketch, "E87.MirrorCS", {"start": v(-15, 120) * mm, "mid": v(0, 135) * mm, "end": v(15, 120) * mm});
            skLineSegment(sketch, "E88.MirrorCS", {"start": v(-15, 120) * mm, "end": v(-15, 108) * mm});
            skPoint(sketch, "E89.endSnap0", {"position": v(80, 0) * mm});
            skLineSegment(sketch, "E90", {"start": v(80, 0) * mm, "end": v(-80, 0) * mm});
            skLineSegment(sketch, "E91.MirrorCS", {"start": v(-15, -108) * mm, "end": v(-33, -90) * mm});
            skLineSegment(sketch, "E92.MirrorCS", {"start": v(-15, -108) * mm, "end": v(-15, -120) * mm});
            skLineSegment(sketch, "E93.MirrorCS", {"start": v(15, -120) * mm, "end": v(15, -108) * mm});
            skLineSegment(sketch, "E94.MirrorCS", {"start": v(15, -108) * mm, "end": v(33, -90) * mm});
            skArc(sketch, "E95.MirrorCS", {"start": v(15, -120) * mm, "mid": v(0, -135) * mm, "end": v(-15, -120) * mm});
            skCircle(sketch, "E96.MirrorC", {"center": v(0, -120) * mm, "radius": 6 * mm});
            skLineSegment(sketch, "E97.MirrorCS", {"start": v(0, -90) * mm, "end": v(0, -120) * mm, "construction": true});
            skSolve(sketch);
        }
        {
            var Q0;
            {var subQ0=sQuery(id+"F16.wireOp",EDGE,"E82");Q0=makeQuery(id+"F16.imprint","IMPRINT",FACE,{"disambiguationData":[TD([[makeQuery(id+"F16.imprint","IMPRINT",EDGE,{"derivedFrom":subQ0}),-1.0]])]});}
            var Q1;
            Q1=makeQuery(id+"F16.imprint","IMPRINT",FACE,{"disambiguationData":[TD([[makeQuery(id+"F16.imprint","IMPRINT",EDGE,{"derivedFrom":makeQuery(id+"F1.opExtrude","CAP_EDGE",EDGE,{"disambiguationData":[OSD([sQuery(id+"F0.wireOp",EDGE,"E4")])],"isStart":true})}),-1.0]])]});
            var Q2;
            Q2=makeQuery(id+"F16.imprint","IMPRINT",FACE,{"disambiguationData":[TD([[makeQuery(id+"F16.imprint","IMPRINT",EDGE,{"derivedFrom":makeQuery(id+"F1.opExtrude","CAP_EDGE",EDGE,{"disambiguationData":[OSD([sQuery(id+"F0.wireOp",EDGE,"E6")])],"isStart":true})}),-1.0]])]});
            var Q3;
            {var subQ1=sQuery(id+"F16.wireOp",EDGE,"E91.MirrorCS");Q3=makeQuery(id+"F16.imprint","IMPRINT",FACE,{"disambiguationData":[TD([[makeQuery(id+"F16.imprint","IMPRINT",EDGE,{"derivedFrom":subQ1}),-1.0]])]});}
            var Q4;
            Q4=makeQuery(id+"F2.opExtrude","CAP_FACE",FACE,{"disambiguationData":[OSD([sQuery(id+"F0.wireOp",EDGE,"E12"),sQuery(id+"F0.wireOp",EDGE,"E13"),sQuery(id+"F0.wireOp",EDGE,"E14"),sQuery(id+"F0.wireOp",EDGE,"E15"),sQuery(id+"F0.wireOp",EDGE,"E17.filletArc"),sQuery(id+"F0.wireOp",EDGE,"E18.filletArc"),sQuery(id+"F0.wireOp",EDGE,"E19.filletArc"),sQuery(id+"F0.wireOp",EDGE,"E20.filletArc"),sQuery(id+"F0.wireOp",EDGE,"E25.0"),sQuery(id+"F0.wireOp",EDGE,"E25.1"),sQuery(id+"F0.wireOp",EDGE,"E25.2"),sQuery(id+"F0.wireOp",EDGE,"E25.3"),sQuery(id+"F0.wireOp",EDGE,"E25.4"),sQuery(id+"F0.wireOp",EDGE,"E25.5"),sQuery(id+"F0.wireOp",EDGE,"E25.6"),sQuery(id+"F0.wireOp",EDGE,"E25.7")])],"isStart":false});
            extrude(context, id + "F17", {"entities" : qUnion([Q0, Q1, Q2, Q3]), "endBound" : BoundingType.UP_TO_SURFACE, "depth" : 25 * mm, "endBoundEntityFace" : qUnion([Q4]), "offsetDistance" : 25 * mm});
        }
    });
